# Revit family: NORDLI 3 RACKS
name_source: partatom
category: Furniture
units: mm (PartAtom-declared; Revit-internal decimal feet)

## family parameters
Always vertical = Yes
Cut with Voids When Loaded = No
OmniClass Number = 23.40.20.00
OmniClass Title = General Furniture and Specialties
Room Calculation Point = No
Shared = No
Work Plane-Based = No

## types (2) — shared parameters
D = 3 mm  [stored 0.00984252 ft]
D/2 = 2 mm  [stored 0.00656168 ft]
Depth = 470 mm  [stored 1.54199 ft]
H = 680 mm  [stored 2.23097 ft]
H1 = 10 mm  [stored 0.0328084 ft]
H2 = 19 mm  [stored 0.062336 ft]
Height = 770 mm  [stored 2.52625 ft]
Radius = 10 mm  [stored 0.0328084 ft]

## per-type parameters (varying)
| type | LMDP | Length |
| 80CM | 26 mm | 800 mm  [stored 2.62467 ft] |
| 40CM | 18 mm  [stored 0.0590551 ft] | 400 mm  [stored 1.31234 ft] |

note: [stored X ft] marks values corroborated as IEEE doubles in the binary element streams (Revit-internal decimal feet)

## geometry (parser evidence)
native form markers: Sweep x2
no freeform markers — native parametric forms only
